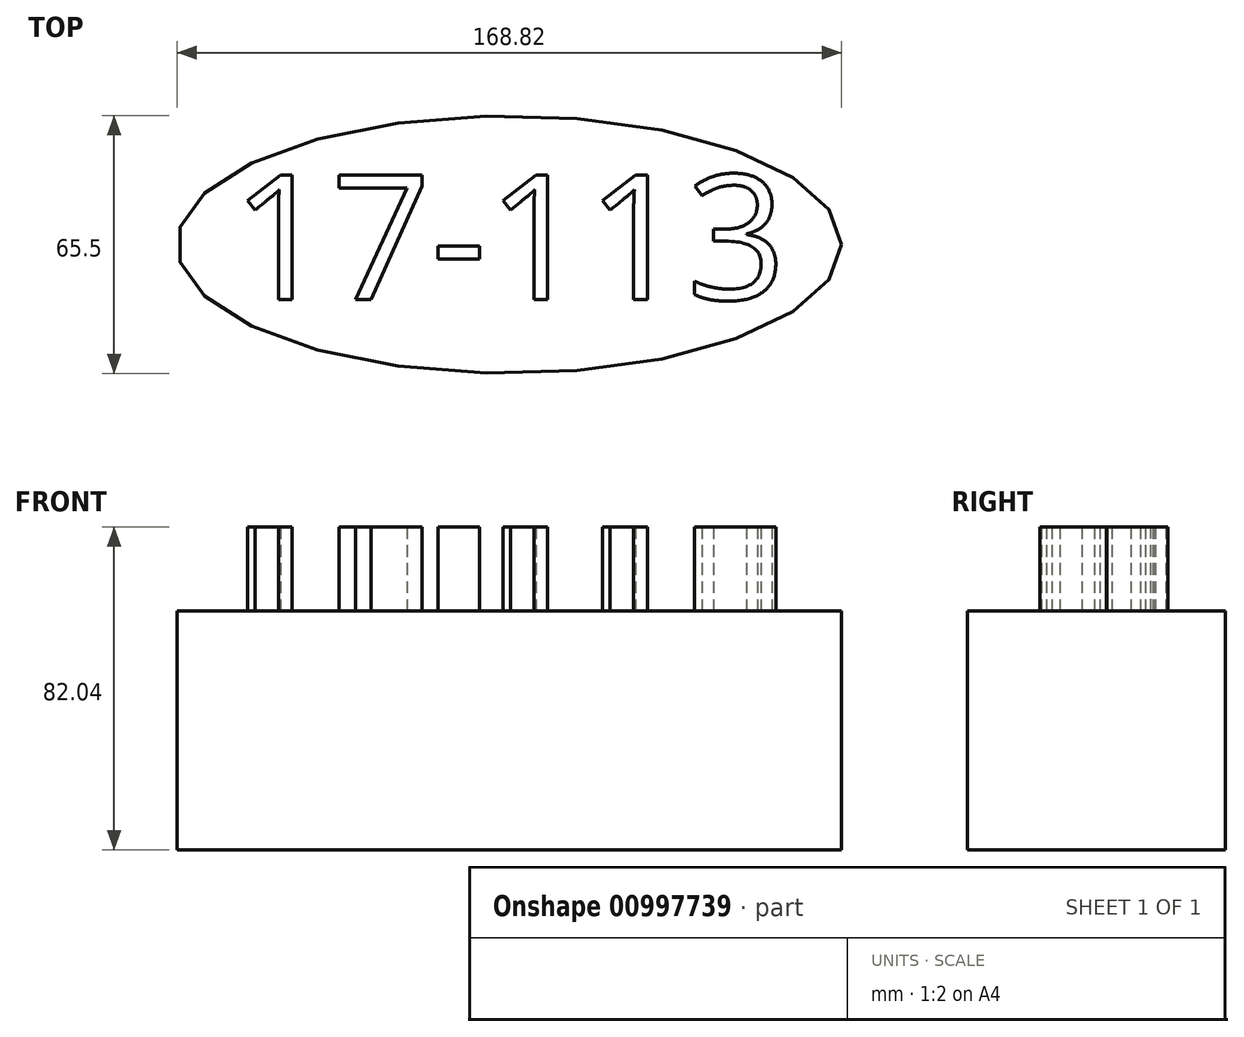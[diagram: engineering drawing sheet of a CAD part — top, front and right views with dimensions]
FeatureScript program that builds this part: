
annotation { "Feature Type Name" : "Feature", "Feature Type Description" : "" }
export const myFeature = defineFeature(function(context is Context, id is Id, definition is map)
    precondition{}
    {
        {
            var Q0;
            Q0=qCreatedBy(makeId("Top.planeOp"),FACE);
            var sketch = newSketch(context, id + "F0", { "sketchPlane" : qUnion([Q0])});
            skEllipse(sketch, "E0", {"center": v(0, 0) * mm, "majorRadius": 84.4 * mm, "minorRadius": 32.75 * mm, "majorAxis": v(1, 0)});
            skSolve(sketch);
        }
        {
            var Q0;
            Q0=makeQuery(id+"F0.imprint","IMPRINT",FACE,{"disambiguationData":[TD([[makeQuery(id+"F0.imprint","IMPRINT",EDGE,{"derivedFrom":sQuery(id+"F0.wireOp",EDGE,"E0")}),1.0]])]});
            var sketch = newSketch(context, id + "F1", { "sketchPlane" : qUnion([Q0])});
            skSolve(sketch);
        }
        {
            var Q0;
            Q0 = qSketchRegion(id + "F1", true);
            var Q1;
            Q1=makeQuery(id+"F1.imprint","IMPRINT",FACE,{"disambiguationData":[TD([[makeQuery(id+"F1.imprint","IMPRINT",EDGE,{"derivedFrom":makeQuery(id+"F0.imprint","IMPRINT",EDGE,{"derivedFrom":sQuery(id+"F0.wireOp",EDGE,"E0")})}),1.0]])]});
            extrude(context, id + "F2", {"entities" : qUnion([Q0, Q1]), "depth" : 25.4 * mm, "offsetDistance" : 25.4 * mm});
        }
        {
            var Q0;
            Q0 = qSketchRegion(id + "F1", true);
            var Q1;
            Q1=makeQuery(id+"F2.opExtrude","CAP_FACE",FACE,{"disambiguationData":[OSD([sQuery(id+"F0.wireOp",EDGE,"E0")])],"isStart":false});
            var Q2;
            Q2=makeQuery(id+"F0.imprint","IMPRINT",FACE,{"disambiguationData":[TD([[makeQuery(id+"F0.imprint","IMPRINT",EDGE,{"derivedFrom":sQuery(id+"F0.wireOp",EDGE,"E0")}),1.0]])]});
            var Q3;
            Q3=makeQuery(id+"F2.opExtrude","CAP_FACE",FACE,{"disambiguationData":[OSD([sQuery(id+"F0.wireOp",EDGE,"E0")])],"isStart":true});
            extrude(context, id + "F3", {"entities" : qUnion([Q0, Q1, Q2, Q3]), "operationType" : NewBodyOperationType.ADD, "depth" : 35.3 * mm, "offsetDistance" : 25.4 * mm});
        }
        {
            var Q0;
            {var subQ0=sQuery(id+"F0.wireOp",EDGE,"E0");Q0=makeQuery(id+"F3.opExtrude","CAP_FACE",FACE,{"disambiguationData":[OSD([subQ0]),TDD([makeQuery(id+"F2.opExtrude","CAP_FACE",FACE,{"disambiguationData":[OSD([subQ0])],"isStart":false})])],"isStart":false});}
            var sketch = newSketch(context, id + "F4", { "sketchPlane" : qUnion([Q0])});
            skText(sketch, "E1", { "text": "17-113", "fontName": "OpenSans-Regular.ttf"});
            const initialGuessF4  = {"E1": [-0.07059, -0.01395, 1, 0, 0.0319]};
            skSetInitialGuess(sketch, initialGuessF4);
            skSolve(sketch);
        }
        {
            var Q0;
            Q0 = qSketchRegion(id + "F4", true);
            extrude(context, id + "F5", {"entities" : qUnion([Q0]), "depth" : 21.34 * mm, "offsetDistance" : 25.4 * mm});
        }
    });
